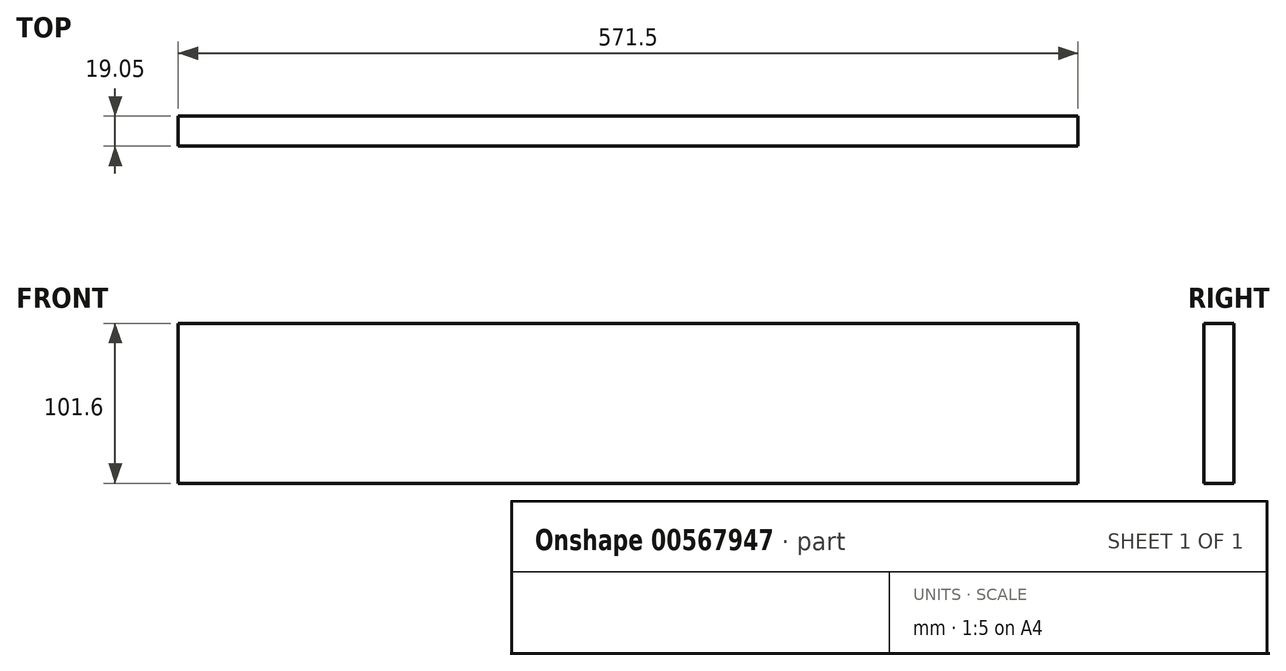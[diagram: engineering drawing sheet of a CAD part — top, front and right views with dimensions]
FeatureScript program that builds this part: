
annotation { "Feature Type Name" : "Feature", "Feature Type Description" : "" }
export const myFeature = defineFeature(function(context is Context, id is Id, definition is map)
    precondition{}
    {
        {
            var Q0;
            Q0=qCreatedBy(makeId("Top.planeOp"),FACE);
            var sketch = newSketch(context, id + "F0", { "sketchPlane" : qUnion([Q0])});
            skLineSegment(sketch, "E0.bottom", {"start": v(0, 0) * mm, "end": v(571.5, 0) * mm});
            skLineSegment(sketch, "E0.top", {"start": v(0, 19.05) * mm, "end": v(571.5, 19.05) * mm});
            skLineSegment(sketch, "E0.left", {"start": v(0, 0) * mm, "end": v(0, 19.05) * mm});
            skLineSegment(sketch, "E0.right", {"start": v(571.5, 0) * mm, "end": v(571.5, 19.05) * mm});
            skSolve(sketch);
        }
        {
            var Q0;
            Q0=makeQuery(id+"F0.imprint","IMPRINT",FACE,{"disambiguationData":[TD([[makeQuery(id+"F0.imprint","IMPRINT",EDGE,{"derivedFrom":sQuery(id+"F0.wireOp",EDGE,"E0.bottom")}),1.0]])]});
            extrude(context, id + "F1", {"entities" : qUnion([Q0]), "depth" : 101.6 * mm, "offsetDistance" : 25.4 * mm});
        }
    });
